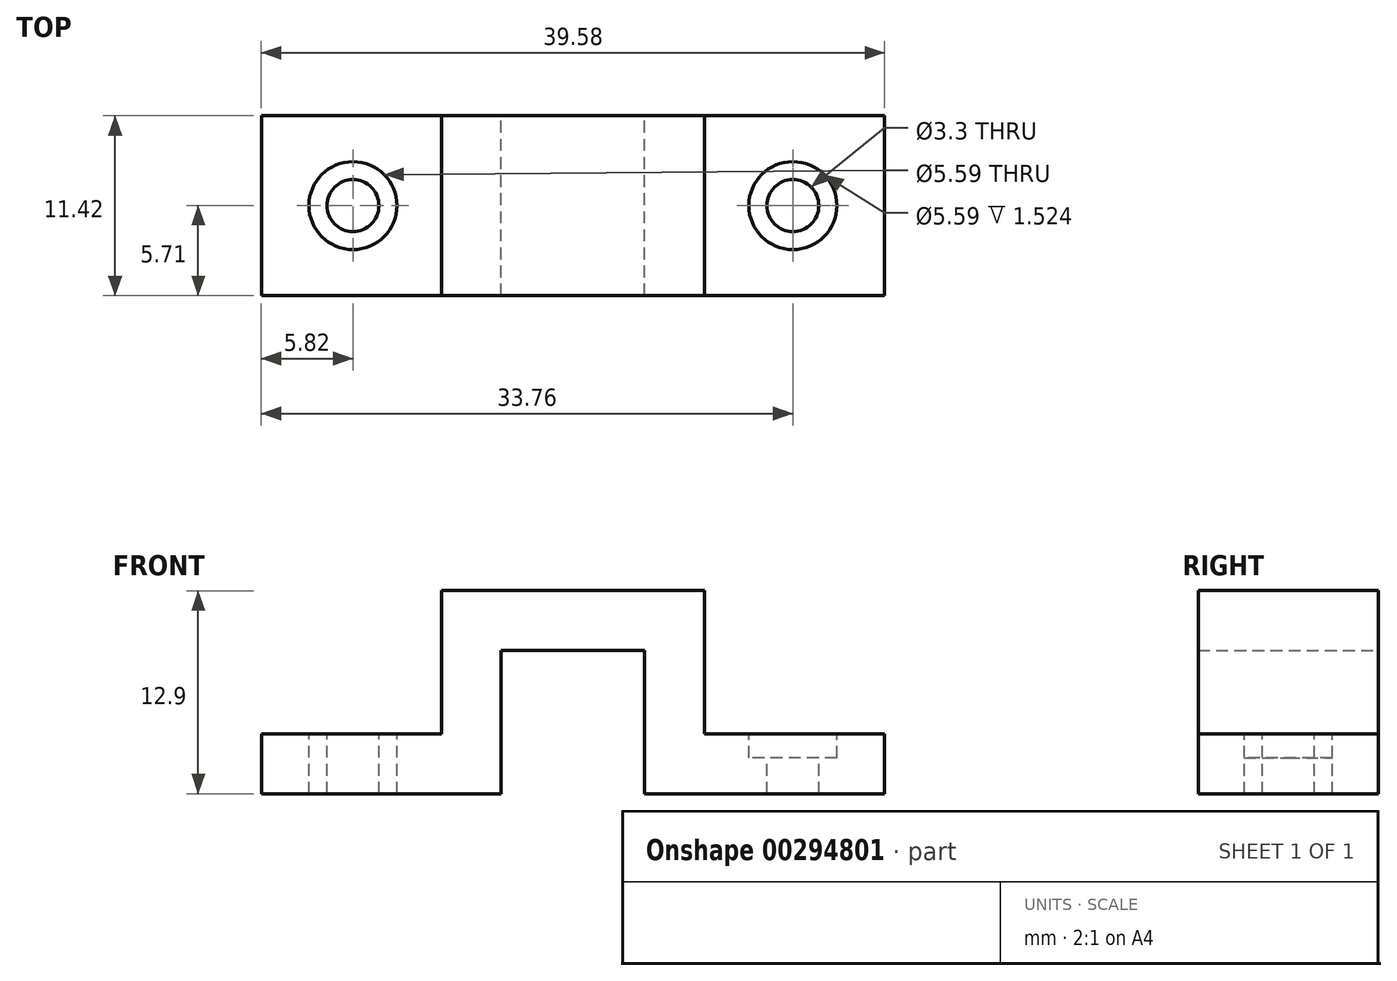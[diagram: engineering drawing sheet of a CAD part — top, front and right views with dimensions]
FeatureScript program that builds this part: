
annotation { "Feature Type Name" : "Feature", "Feature Type Description" : "" }
export const myFeature = defineFeature(function(context is Context, id is Id, definition is map)
    precondition{}
    {
        {
            var Q0;
            Q0=qCreatedBy(makeId("Front.planeOp"),FACE);
            var sketch = newSketch(context, id + "F0", { "sketchPlane" : qUnion([Q0])});
            skLineSegment(sketch, "E0", {"start": v(-19.79, 0) * mm, "end": v(-4.55, 0) * mm});
            skLineSegment(sketch, "E1", {"start": v(-4.55, 0) * mm, "end": v(-4.55, 9.1) * mm});
            skLineSegment(sketch, "E2", {"start": v(-4.55, 9.1) * mm, "end": v(4.55, 9.1) * mm});
            skLineSegment(sketch, "E3", {"start": v(4.55, 9.1) * mm, "end": v(4.55, 0) * mm});
            skLineSegment(sketch, "E4", {"start": v(4.55, 0) * mm, "end": v(19.79, 0) * mm});
            skLineSegment(sketch, "E5.0", {"start": v(8.36, 3.81) * mm, "end": v(19.79, 3.81) * mm});
            skLineSegment(sketch, "E5.1", {"start": v(-19.79, 3.81) * mm, "end": v(-8.36, 3.81) * mm});
            skLineSegment(sketch, "E5.2", {"start": v(-8.36, 3.81) * mm, "end": v(-8.36, 12.9) * mm});
            skLineSegment(sketch, "E5.3", {"start": v(-8.36, 12.9) * mm, "end": v(8.36, 12.9) * mm});
            skLineSegment(sketch, "E5.4", {"start": v(8.36, 12.9) * mm, "end": v(8.36, 3.81) * mm});
            skLineSegment(sketch, "E6", {"start": v(-19.79, 3.81) * mm, "end": v(-19.79, 0) * mm});
            skLineSegment(sketch, "E7", {"start": v(19.79, 3.81) * mm, "end": v(19.79, 0) * mm});
            skSolve(sketch);
        }
        {
            var Q0;
            Q0 = qSketchRegion(id + "F0", true);
            extrude(context, id + "F1", {"entities" : qUnion([Q0]), "endBound" : BoundingType.SYMMETRIC, "depth" : 11.43 * mm});
        }
        {
            var Q0;
            Q0=makeQuery(id+"F1.opExtrude","SWEPT_FACE",FACE,{"disambiguationData":[OSD([sQuery(id+"F0.wireOp",EDGE,"E5.0")])]});
            var sketch = newSketch(context, id + "F2", { "sketchPlane" : qUnion([Q0])});
            skCircle(sketch, "E8", {"center": v(13.97, 0) * mm, "radius": 2.8 * mm});
            skCircle(sketch, "E9", {"center": v(13.97, 0) * mm, "radius": 1.65 * mm});
            skCircle(sketch, "E10.MirrorC", {"center": v(-13.97, 0) * mm, "radius": 2.8 * mm});
            skCircle(sketch, "E11.MirrorC", {"center": v(-13.97, 0) * mm, "radius": 1.65 * mm});
            skSolve(sketch);
        }
        {
            var Q0;
            Q0=makeQuery(id+"F2.imprint","IMPRINT",FACE,{"disambiguationData":[TD([[makeQuery(id+"F2.imprint","IMPRINT",EDGE,{"derivedFrom":sQuery(id+"F2.wireOp",EDGE,"E11.MirrorC")}),-1.0]])]});
            var Q1;
            Q1=makeQuery(id+"F2.imprint","IMPRINT",FACE,{"disambiguationData":[TD([[makeQuery(id+"F2.imprint","IMPRINT",EDGE,{"derivedFrom":sQuery(id+"F2.wireOp",EDGE,"E9")}),1.0]])]});
            extrude(context, id + "F3", {"entities" : qUnion([Q0, Q1]), "operationType" : NewBodyOperationType.REMOVE, "endBound" : BoundingType.THROUGH_ALL, "oppositeDirection" : true, "depth" : 25.4 * mm});
        }
        {
            var Q0;
            Q0 = qSketchRegion(id + "F2", true);
            extrude(context, id + "F4", {"entities" : qUnion([Q0]), "operationType" : NewBodyOperationType.REMOVE, "oppositeDirection" : true, "depth" : 1.52 * mm});
        }
    });
